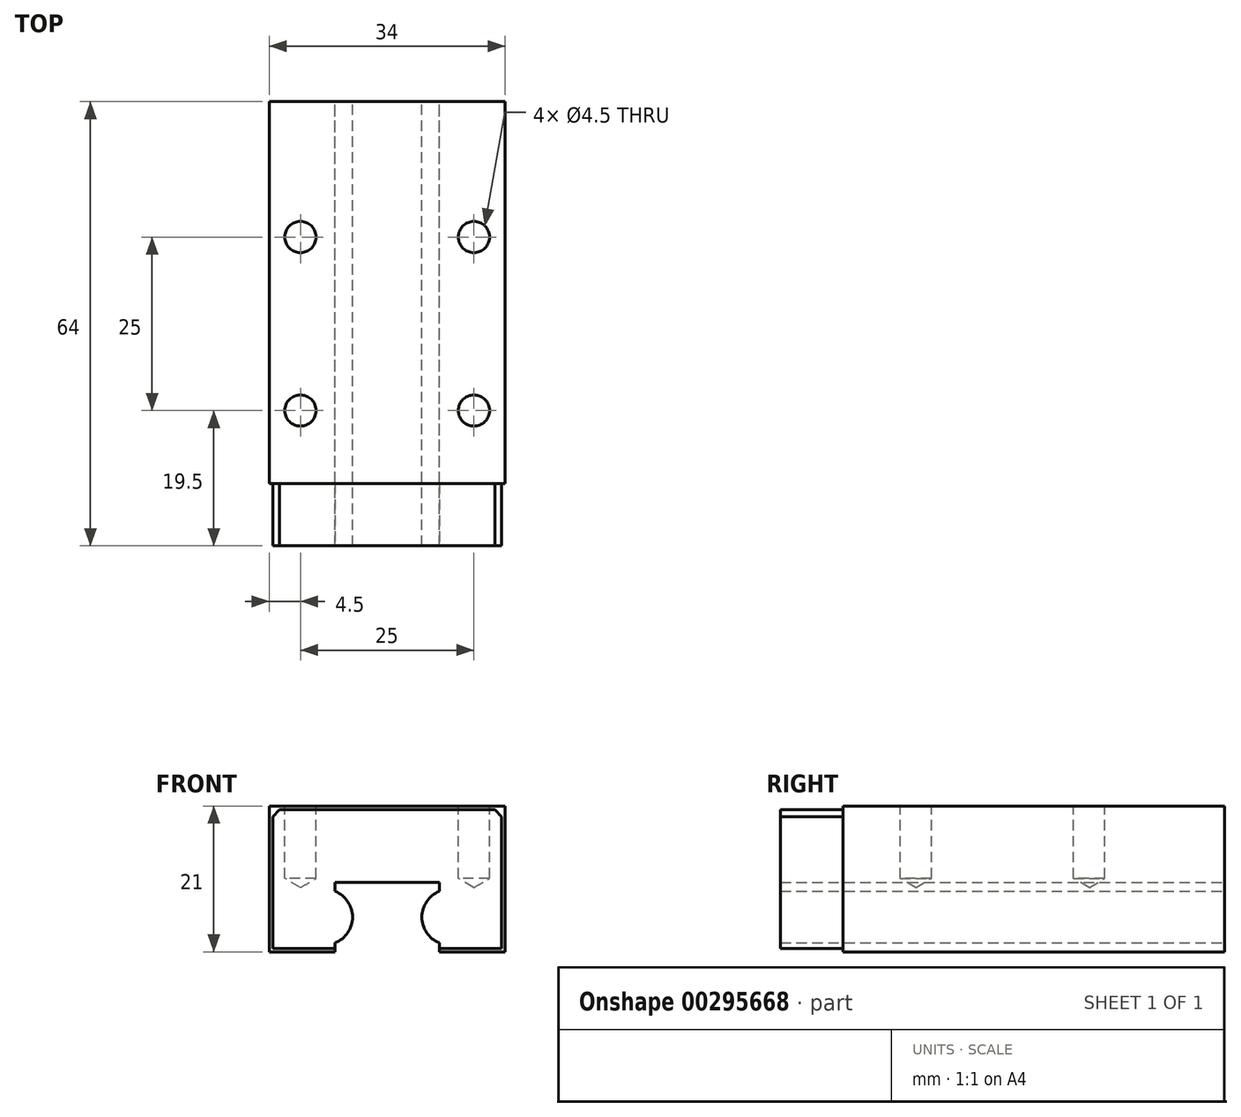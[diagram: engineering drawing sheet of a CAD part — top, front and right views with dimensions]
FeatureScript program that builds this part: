
annotation { "Feature Type Name" : "Feature", "Feature Type Description" : "" }
export const myFeature = defineFeature(function(context is Context, id is Id, definition is map)
    precondition{}
    {
        {
            var Q0;
            Q0=qCreatedBy(makeId("Front.planeOp"),FACE);
            var sketch = newSketch(context, id + "F0", { "sketchPlane" : qUnion([Q0])});
            skLineSegment(sketch, "E0.bottom", {"start": v(-17, 0) * mm, "end": v(-7.5, 0) * mm});
            skLineSegment(sketch, "E0.top", {"start": v(-17, 21) * mm, "end": v(17, 21) * mm});
            skLineSegment(sketch, "E0.left", {"start": v(-17, 0) * mm, "end": v(-17, 21) * mm});
            skLineSegment(sketch, "E0.right", {"start": v(17, 0) * mm, "end": v(17, 21) * mm});
            skLineSegment(sketch, "E1", {"start": v(0, 21) * mm, "end": v(0, 0) * mm, "construction": true});
            skLineSegment(sketch, "E2.top", {"start": v(-7.5, 10) * mm, "end": v(7.5, 10) * mm});
            skLineSegment(sketch, "E2.left", {"start": v(-7.5, 0) * mm, "end": v(-7.5, 1.3) * mm});
            skLineSegment(sketch, "E2.right", {"start": v(7.5, 0) * mm, "end": v(7.5, 1.3) * mm});
            skArc(sketch, "E3", {"start": v(-7.5, 1.3) * mm, "mid": v(-5, 5) * mm, "end": v(-7.5, 8.7) * mm});
            skPoint(sketch, "E3.centerSnap0", {"position": v(-7.5, 5) * mm});
            skArc(sketch, "E4", {"start": v(7.5, 8.7) * mm, "mid": v(5, 5) * mm, "end": v(7.5, 1.3) * mm});
            skLineSegment(sketch, "E5.trimOffspring", {"start": v(-7.5, 8.7) * mm, "end": v(-7.5, 10) * mm});
            skLineSegment(sketch, "E6.trimOffspring", {"start": v(7.5, 8.7) * mm, "end": v(7.5, 10) * mm});
            skLineSegment(sketch, "E7.trimOffspring", {"start": v(7.5, 0) * mm, "end": v(17, 0) * mm});
            skSolve(sketch);
        }
        {
            var Q0;
            Q0 = qSketchRegion(id + "F0", true);
            extrude(context, id + "F1", {"entities" : qUnion([Q0]), "endBound" : BoundingType.SYMMETRIC, "depth" : 64 * mm});
        }
        {
            var Q0;
            Q0=makeQuery(id+"F1.opExtrude","CAP_FACE",FACE,{"disambiguationData":[OSD([sQuery(id+"F0.wireOp",EDGE,"E0.bottom"),sQuery(id+"F0.wireOp",EDGE,"E0.top"),sQuery(id+"F0.wireOp",EDGE,"E0.left"),sQuery(id+"F0.wireOp",EDGE,"E0.right"),sQuery(id+"F0.wireOp",EDGE,"E2.top"),sQuery(id+"F0.wireOp",EDGE,"E2.left"),sQuery(id+"F0.wireOp",EDGE,"E2.right"),sQuery(id+"F0.wireOp",EDGE,"E3"),sQuery(id+"F0.wireOp",EDGE,"E4"),sQuery(id+"F0.wireOp",EDGE,"E5.trimOffspring"),sQuery(id+"F0.wireOp",EDGE,"E6.trimOffspring"),sQuery(id+"F0.wireOp",EDGE,"E7.trimOffspring")])],"isStart":false});
            var sketch = newSketch(context, id + "F2", { "sketchPlane" : qUnion([Q0])});
            skLineSegment(sketch, "E8.bottom", {"start": v(-17, 21) * mm, "end": v(17, 21) * mm});
            skLineSegment(sketch, "E8.top", {"start": v(-17, 0) * mm, "end": v(17, 0) * mm});
            skLineSegment(sketch, "E8.left", {"start": v(-17, 21) * mm, "end": v(-17, 0) * mm});
            skLineSegment(sketch, "E8.right", {"start": v(17, 21) * mm, "end": v(17, 0) * mm});
            skLineSegment(sketch, "E9.0", {"start": v(-15.5, 20.5) * mm, "end": v(15.5, 20.5) * mm});
            skLineSegment(sketch, "E9.1", {"start": v(-16.5, 19.5) * mm, "end": v(-16.5, 0.5) * mm});
            skLineSegment(sketch, "E9.2", {"start": v(-16.5, 0.5) * mm, "end": v(16.5, 0.5) * mm});
            skLineSegment(sketch, "E9.3", {"start": v(16.5, 19.5) * mm, "end": v(16.5, 0.5) * mm});
            skLineSegment(sketch, "E10", {"start": v(15.5, 20.5) * mm, "end": v(16.5, 19.5) * mm});
            skLineSegment(sketch, "E11", {"start": v(-16.5, 19.5) * mm, "end": v(-15.5, 20.5) * mm});
            skLineSegment(sketch, "E12", {"start": v(0, 20.5) * mm, "end": v(0, 0.5) * mm, "construction": true});
            skPoint(sketch, "E13.orphan", {"position": v(-16.5, 20.5) * mm});
            skPoint(sketch, "E14.orphan", {"position": v(16.5, 20.5) * mm});
            skSolve(sketch);
        }
        {
            var Q0;
            Q0 = qSketchRegion(id + "F2", true);
            extrude(context, id + "F3", {"entities" : qUnion([Q0]), "operationType" : NewBodyOperationType.REMOVE, "oppositeDirection" : true, "depth" : 9 * mm});
        }
        {
            var Q0;
            Q0=makeQuery(id+"F1.opExtrude","SWEPT_FACE",FACE,{"disambiguationData":[OSD([sQuery(id+"F0.wireOp",EDGE,"E0.top")])]});
            var sketch = newSketch(context, id + "F4", { "sketchPlane" : qUnion([Q0])});
            skLineSegment(sketch, "E15", {"start": v(-17, 0) * mm, "end": v(17, 0) * mm, "construction": true});
            skLineSegment(sketch, "E16", {"start": v(0, 23) * mm, "end": v(0, -23) * mm, "construction": true});
            skLineSegment(sketch, "E17.bottom", {"start": v(-12.5, 12.5) * mm, "end": v(12.5, 12.5) * mm, "construction": true});
            skLineSegment(sketch, "E17.top", {"start": v(-12.5, -12.5) * mm, "end": v(12.5, -12.5) * mm, "construction": true});
            skLineSegment(sketch, "E17.left", {"start": v(-12.5, 12.5) * mm, "end": v(-12.5, -12.5) * mm, "construction": true});
            skLineSegment(sketch, "E17.right", {"start": v(12.5, 12.5) * mm, "end": v(12.5, -12.5) * mm, "construction": true});
            skPoint(sketch, "E18", {"position": v(-12.5, 12.5) * mm});
            skPoint(sketch, "E19", {"position": v(12.5, 12.5) * mm});
            skPoint(sketch, "E20", {"position": v(12.5, -12.5) * mm});
            skPoint(sketch, "E21", {"position": v(-12.5, -12.5) * mm});
            skSolve(sketch);
        }
        {
            var Q0;
            Q0=sQuery(id+"F4.wireOp",VERTEX,"E18");
            var Q1;
            Q1=sQuery(id+"F4.wireOp",VERTEX,"E19");
            var Q2;
            Q2=sQuery(id+"F4.wireOp",VERTEX,"E20");
            var Q3;
            Q3=sQuery(id+"F4.wireOp",VERTEX,"E21");
            var Q4;
            Q4=makeQuery(id+"F1.opExtrude","SWEPT_BODY",BODY,{"disambiguationData":[OSD([sQuery(id+"F0.wireOp",EDGE,"E0.bottom"),sQuery(id+"F0.wireOp",EDGE,"E0.top"),sQuery(id+"F0.wireOp",EDGE,"E0.left"),sQuery(id+"F0.wireOp",EDGE,"E0.right"),sQuery(id+"F0.wireOp",EDGE,"E2.top"),sQuery(id+"F0.wireOp",EDGE,"E2.left"),sQuery(id+"F0.wireOp",EDGE,"E2.right"),sQuery(id+"F0.wireOp",EDGE,"E3"),sQuery(id+"F0.wireOp",EDGE,"E4"),sQuery(id+"F0.wireOp",EDGE,"E5.trimOffspring"),sQuery(id+"F0.wireOp",EDGE,"E6.trimOffspring"),sQuery(id+"F0.wireOp",EDGE,"E7.trimOffspring")])]});
            hole(context, id + "F5", {"style" : HoleStyle.SIMPLE, "endStyle" : HoleEndStyle.BLIND, "standardTappedOrClearance" : lookupTablePath({ "standard" : "ISO", "engagement" : "25%", "pitch" : "0.8 mm", "size" : "M5", "type" : "Tapped" }), "standardBlindInLast" : lookupTablePath({ "standard" : "ISO", "engagement" : "25%", "pitch" : "0.8 mm", "size" : "M5", "type" : "Tapped" }), "holeDiameter" : 4.5 * mm, "showTappedDepth" : true, "holeDepth" : 10.4 * mm, "tappedDepth" : 8 * mm, "tapClearance" : 3, "locations" : qUnion([Q0, Q1, Q2, Q3]), "scope" : qUnion([Q4])});
        }
    });
